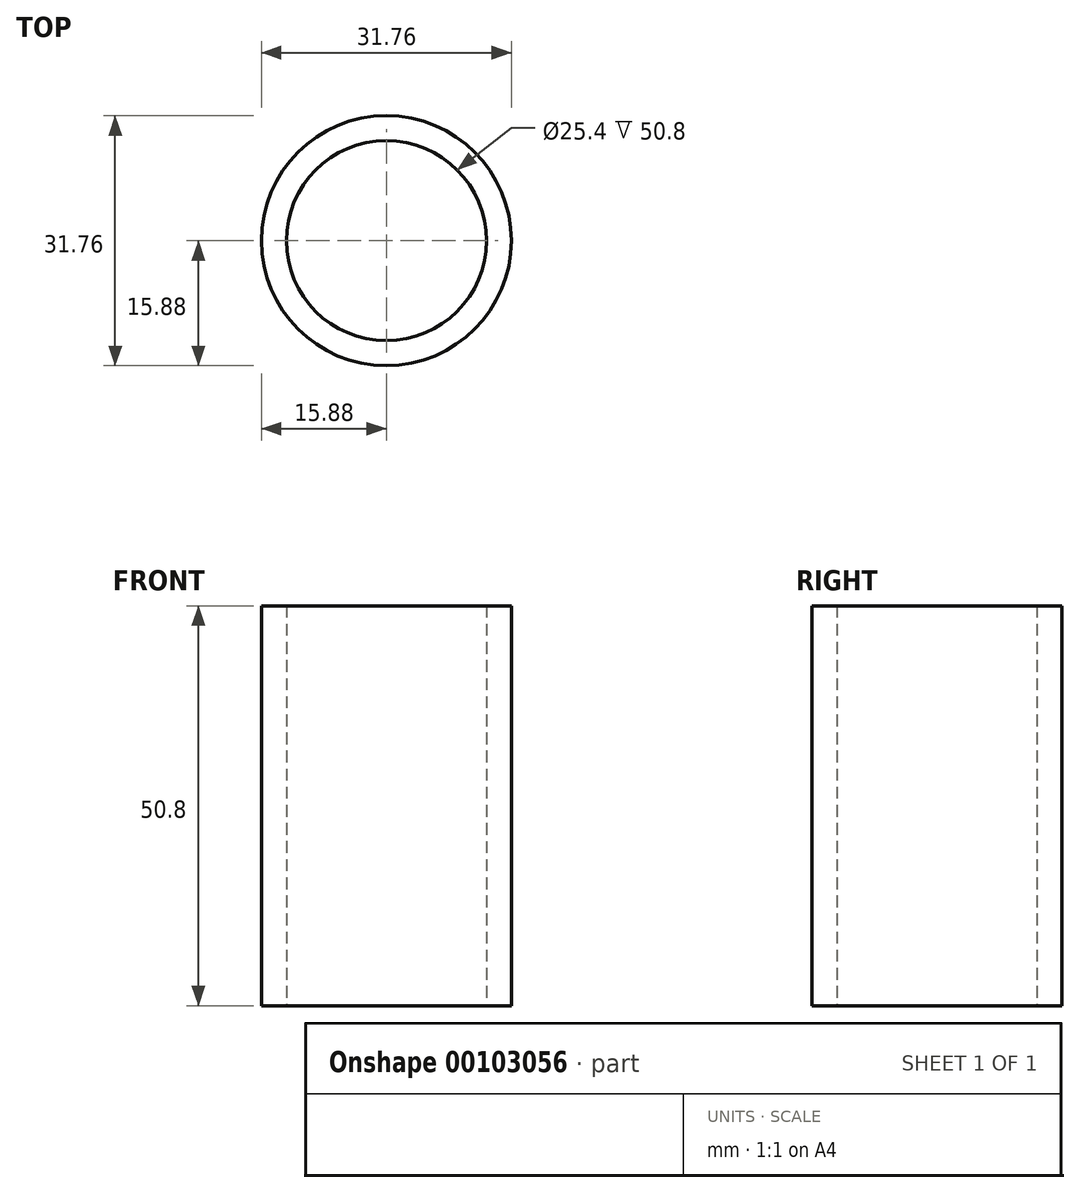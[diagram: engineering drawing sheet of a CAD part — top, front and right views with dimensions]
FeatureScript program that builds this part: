
annotation { "Feature Type Name" : "Feature", "Feature Type Description" : "" }
export const myFeature = defineFeature(function(context is Context, id is Id, definition is map)
    precondition{}
    {
        {
            var Q0;
            Q0=qCreatedBy(makeId("Top.planeOp"),FACE);
            var sketch = newSketch(context, id + "F0", { "sketchPlane" : qUnion([Q0])});
            skCircle(sketch, "E0", {"center": v(0, 0) * mm, "radius": 15.88 * mm});
            skCircle(sketch, "E1", {"center": v(0, 0) * mm, "radius": 12.7 * mm});
            skSolve(sketch);
        }
        {
            var Q0;
            Q0=makeQuery(id+"F0.imprint","IMPRINT",FACE,{"disambiguationData":[TD([[makeQuery(id+"F0.imprint","IMPRINT",EDGE,{"derivedFrom":sQuery(id+"F0.wireOp",EDGE,"E0")}),1.0]])]});
            extrude(context, id + "F1", {"entities" : qUnion([Q0]), "depth" : 50.8 * mm});
        }
    });
